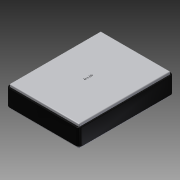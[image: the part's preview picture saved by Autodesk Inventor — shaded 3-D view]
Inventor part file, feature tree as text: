
AUTODESK INVENTOR PART (.ipt)
format: ipt  version: 2013 (Build 170138000, 138)  size: 461,824 bytes
history: native  units: mm
features: fillet x3, sketch x3, extrude x2, emboss x1
ambient origin geometry x8: Origin, YZ Plane, XZ Plane, XY Plane, X Axis, Y Axis, Z Axis, Center Point
feature tree (9):
  extrude  "Extrusion1"  Depth=111.76mm
  extrude  "Extrusion2"  Depth=2.54mm
  fillet  "Fillet1"  Radius=2.54mm
  fillet  "Fillet2"  Radius=33.02mm
  fillet  "Fillet3"  Radius=0.508mm
  emboss  "Emboss1"
  sketch  "Sketch1"  dims[d0=144.78mm d1=111.76mm]
  sketch  "Sketch2"  dims[d2=25.4mm d3=0.0mm d4=2.54mm d5=2.54mm d6=33.02mm d7=0.0mm d8=0.508mm]
  sketch  "Sketch3"  dims[d9=1.27mm d11=2.54mm d12=2.54mm d13=5.08mm d14=2.54mm d15=0.0mm]
